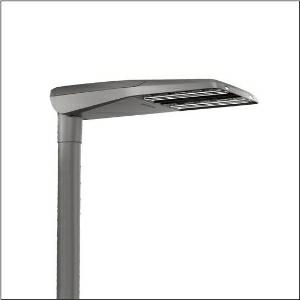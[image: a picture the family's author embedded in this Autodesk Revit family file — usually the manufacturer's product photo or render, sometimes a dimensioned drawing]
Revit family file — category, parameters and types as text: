
# Revit family: streetlight_sl_11_iq_midi___st1_2a_5xc3a41f08le_475e
name_source: partatom
category: Lighting Fixtures
units: mm (PartAtom-declared; Revit-internal decimal feet)

## family parameters
Cut with Voids When Loaded = No
Host = Face
Light Source = No
Part Type = Normal
Room Calculation Point = No
Round Connector Dimension = Use Diameter
Shared = No

## types (1)
- --- (1 x LED, 9590 lm, 60.4 W, 4000K)
    Apparent Load = 60 VA
    CIE Flux Codes = 32 70 96 100 100
    Color Rendering = 70
    Color Temperature = 4000K
    Default Elevation = 1800 mm
    Description = Streetlight SL 11 iQ midi, mast luminaire, primary light control with 3 zone facetted reflector, of plastic, silver coated, highly specular, primary optical cover: cover, of PMMA, transparent, light distribution: ST1.2a, light emission: direct distribution, primary light characteristic: asymmetric, installation type: post-top, side-entry, lamps: LED, High Power LED, rated values: 9.590lm | 60,4W | 158,8lm/W (begin service life); end service life: 9.590lm | 62,5W; at 50% lumin. flux: 4.795lm | 29,7W | 161,4lm/W, colour temperature: 4000K, colour rendering: CRI > 70, light colour: 740, light setting 1 begin service life: 100% | 9.590lm | 60,4W | 158,8lm/W | 4.000K, light setting 1 end service life: 62,5W, further light settings possible, control: Street-Remote, optimised constant luminous flux control (CLO 2.0), Desk-Remote (wireless, voltage-free reading and setting of iQ features in the workshop via application-optimized NFC function/RFID function), Light-Fading, Smart-Wire, Night-Set, Lumen-Switch, Temp-Guard, Auto-Match, with cable H07RN-F 5x 1.5mm², mains connection: 230..240V, AC, 50/60Hz, connection cable pre-assembled, cable length: 8,5m, luminaire housing, of diecast aluminium, powder-coated, Siteco® metallic grey (DB 702S), please order mast flange separately, inclination adjustable without tools: 0°, 5°, 10°, 15° (post-top) | 0°, -5°, -10°, -15° (side-entry), sealing non-destructively replaceable, multi-level sealing system, length: 780mm, width: 376mm, height: 118mm, mast flange for spigot size: 42mm (side-entry): 5XC10008XM4, 60/48mm (side-entry/post-top): 5XC10108XM2, 76/60mm (side-entry/post-top): 5XC10108XM1, equipment: standard, protection rating (complete): IP66, insulation class (complete): insulation class II (safety insulation), certification: CE, ENEC, ENEC+, VDE, impact resistance: IK10, permissible operating ambient temperature for outdoor applications: -25..+50°C, standard-compliant lighting for roads and squares, Environmental Product Declaration (EPD) tested and certified by an independent institute, packaging unit: 1 piece

Light Distribution: ST1.2a
    Height = 118 mm
    Lamp = 1 x LED
    Lamp Light Flux = 9590 lm
    Lamp Power = 60.4 W
    Lamp count = 1
    Length = 780 mm
    Luminous efficacy = 159 lm/W
    Manufacturer = Siteco
    ModVariant = No
    Model = 5XC3A41F08LE
    Number of Poles = 1
    OnlyDefault = Yes
    Power Factor = 1
    Product Name = Streetlight SL 11 iQ midi | ST1.2a
    Product group = mast luminaire | pylon top
    ProductGroupID = 6100
    Protection Class = Protection class II
    Protection Degree = IP 66
    RLX_Detail_Level = 1
    RLX_Emergency_Light_Flux = 0 lm
    RLX_Emergency_Type = 0
    RLX_Emergency_Type_DB = No
    RlxData = <blob elided: 70809 chars, md5=7bf68c36>
    Socket = socket
    Standby Power = 0 W
    System Light Flux = 9590 lm
    System Power = 60 W
    Type Comments = factory setting: luminous flux: 100 % | dim-lin: 254 | 520 mA
    Type Image = l_1005960.jpg
    URL = http://relux.com
    VarID = @adj_218317
    Voltage = 0 V
    Weight = 0.00 kg
    Width = 376 mm

## geometry (parser evidence)
native form markers: Blend x4, Sweep x10
no freeform markers — native parametric forms only
